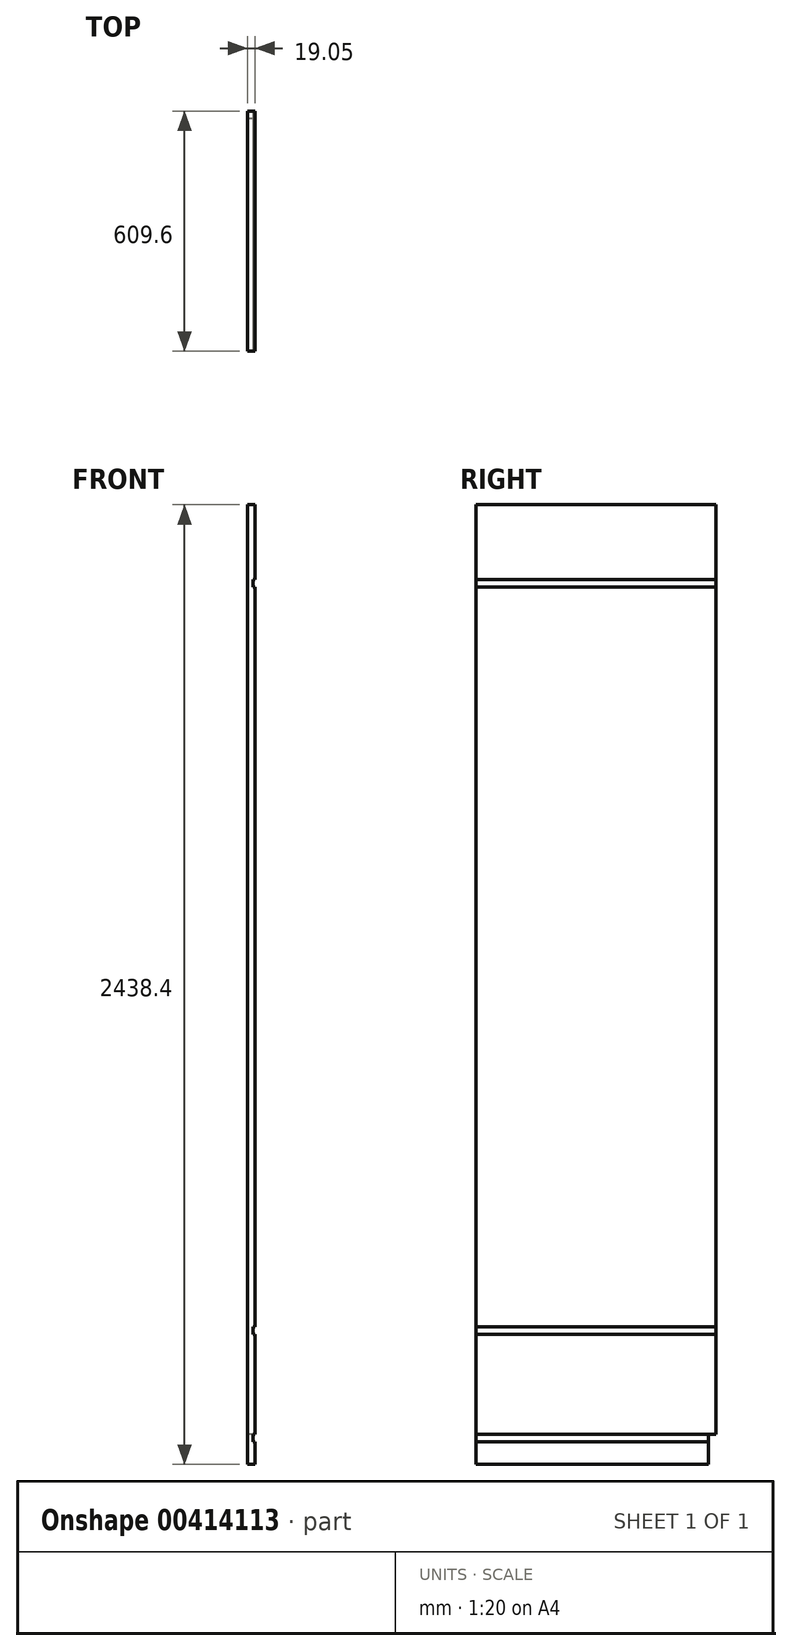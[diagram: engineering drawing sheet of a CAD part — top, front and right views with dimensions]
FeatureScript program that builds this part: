
annotation { "Feature Type Name" : "Feature", "Feature Type Description" : "" }
export const myFeature = defineFeature(function(context is Context, id is Id, definition is map)
    precondition{}
    {
        {
            var Q0;
            Q0=qCreatedBy(makeId("Front.planeOp"),FACE);
            var sketch = newSketch(context, id + "F0", { "sketchPlane" : qUnion([Q0])});
            skLineSegment(sketch, "E0", {"start": v(0, 0) * mm, "end": v(0, 2438.4) * mm});
            skLineSegment(sketch, "E1", {"start": v(0, 2438.4) * mm, "end": v(19.05, 2438.4) * mm});
            skLineSegment(sketch, "E2", {"start": v(19.05, 2438.4) * mm, "end": v(19.05, 0) * mm});
            skLineSegment(sketch, "E3", {"start": v(19.05, 0) * mm, "end": v(0, 0) * mm});
            skSolve(sketch);
        }
        {
            var Q0;
            Q0=makeQuery(id+"F0.imprint","IMPRINT",FACE,{"disambiguationData":[TD([[makeQuery(id+"F0.imprint","IMPRINT",EDGE,{"derivedFrom":sQuery(id+"F0.wireOp",EDGE,"E0")}),-1.0]])]});
            extrude(context, id + "F1", {"entities" : qUnion([Q0]), "oppositeDirection" : true, "depth" : 609.6 * mm});
        }
        {
            var Q0;
            Q0=makeQuery(id+"F1.opExtrude","SWEPT_FACE",FACE,{"disambiguationData":[OSD([sQuery(id+"F0.wireOp",EDGE,"E0")])]});
            var sketch = newSketch(context, id + "F2", { "sketchPlane" : qUnion([Q0])});
            skLineSegment(sketch, "E4", {"start": v(-609.6, 76.2) * mm, "end": v(-590.55, 76.2) * mm});
            skLineSegment(sketch, "E5", {"start": v(-590.55, 76.2) * mm, "end": v(-590.55, 0) * mm});
            skLineSegment(sketch, "E6", {"start": v(-590.55, 0) * mm, "end": v(-609.6, 0) * mm});
            skLineSegment(sketch, "E7", {"start": v(-609.6, 0) * mm, "end": v(-609.6, 76.2) * mm});
            skSolve(sketch);
        }
        {
            var Q0;
            Q0 = qSketchRegion(id + "F2", true);
            extrude(context, id + "F3", {"entities" : qUnion([Q0]), "operationType" : NewBodyOperationType.REMOVE, "endBound" : BoundingType.THROUGH_ALL, "oppositeDirection" : true, "depth" : 25.4 * mm});
        }
        {
            var Q0;
            Q0=makeQuery(id+"F1.opExtrude","CAP_FACE",FACE,{"disambiguationData":[OSD([sQuery(id+"F0.wireOp",EDGE,"E0"),sQuery(id+"F0.wireOp",EDGE,"E1"),sQuery(id+"F0.wireOp",EDGE,"E2"),sQuery(id+"F0.wireOp",EDGE,"E3")])],"isStart":true});
            var sketch = newSketch(context, id + "F4", { "sketchPlane" : qUnion([Q0])});
            skLineSegment(sketch, "E8.bottom", {"start": v(19.05, 76.2) * mm, "end": v(14.29, 76.2) * mm});
            skLineSegment(sketch, "E8.top", {"start": v(19.05, 57.15) * mm, "end": v(14.29, 57.15) * mm});
            skLineSegment(sketch, "E8.left", {"start": v(19.05, 76.2) * mm, "end": v(19.05, 57.15) * mm});
            skLineSegment(sketch, "E8.right", {"start": v(14.29, 76.2) * mm, "end": v(14.29, 57.15) * mm});
            skLineSegment(sketch, "E9.bottom", {"start": v(19.05, 349.25) * mm, "end": v(14.29, 349.25) * mm});
            skLineSegment(sketch, "E9.top", {"start": v(19.05, 330.2) * mm, "end": v(14.29, 330.2) * mm});
            skLineSegment(sketch, "E9.left", {"start": v(19.05, 349.25) * mm, "end": v(19.05, 330.2) * mm});
            skLineSegment(sketch, "E9.right", {"start": v(14.29, 349.25) * mm, "end": v(14.29, 330.2) * mm});
            skLineSegment(sketch, "E10.bottom", {"start": v(19.05, 2247.9) * mm, "end": v(14.29, 2247.9) * mm});
            skLineSegment(sketch, "E10.top", {"start": v(19.05, 2228.85) * mm, "end": v(14.29, 2228.85) * mm});
            skLineSegment(sketch, "E10.left", {"start": v(19.05, 2247.9) * mm, "end": v(19.05, 2228.85) * mm});
            skLineSegment(sketch, "E10.right", {"start": v(14.29, 2247.9) * mm, "end": v(14.29, 2228.85) * mm});
            skSolve(sketch);
        }
        {
            var Q0;
            Q0 = qSketchRegion(id + "F4", true);
            extrude(context, id + "F5", {"entities" : qUnion([Q0]), "operationType" : NewBodyOperationType.REMOVE, "endBound" : BoundingType.THROUGH_ALL, "oppositeDirection" : true, "depth" : 25.4 * mm});
        }
    });
